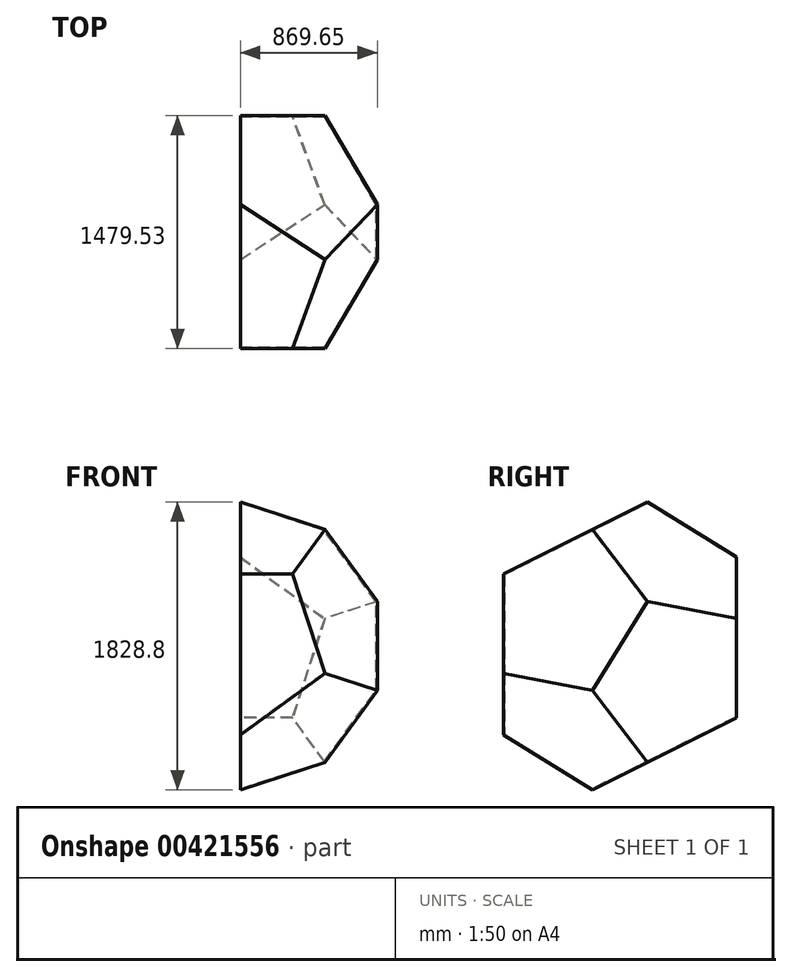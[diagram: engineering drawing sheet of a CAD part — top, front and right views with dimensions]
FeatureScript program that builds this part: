
annotation { "Feature Type Name" : "Feature", "Feature Type Description" : "" }
export const myFeature = defineFeature(function(context is Context, id is Id, definition is map)
    precondition{}
    {
        {
            var Q0;
            Q0=qCreatedBy(makeId("Front.planeOp"),FACE);
            var sketch = newSketch(context, id + "F0", { "sketchPlane" : qUnion([Q0])});
            skCircle(sketch, "E0.cCircle", {"center": v(0, 0) * mm, "radius": 1196.97 * mm, "construction": true});
            skLineSegment(sketch, "E0.0", {"start": v(1407.12, -457.2) * mm, "end": v(0, -1479.53) * mm});
            skLineSegment(sketch, "E0.1", {"start": v(0, -1479.53) * mm, "end": v(-1407.12, -457.2) * mm});
            skLineSegment(sketch, "E0.2", {"start": v(-1407.12, -457.2) * mm, "end": v(-869.65, 1196.97) * mm});
            skLineSegment(sketch, "E0.3", {"start": v(-869.65, 1196.97) * mm, "end": v(869.65, 1196.97) * mm});
            skLineSegment(sketch, "E0.4", {"start": v(869.65, 1196.97) * mm, "end": v(1407.12, -457.2) * mm});
            skLineSegment(sketch, "E1", {"start": v(-1407.12, -457.2) * mm, "end": v(1407.12, -457.2) * mm, "construction": true});
            skLineSegment(sketch, "E2", {"start": v(-1407.12, -457.2) * mm, "end": v(869.65, 1196.97) * mm, "construction": true});
            skLineSegment(sketch, "E3", {"start": v(-869.65, 1196.97) * mm, "end": v(0, -1479.53) * mm, "construction": true});
            skLineSegment(sketch, "E4", {"start": v(869.65, 1196.97) * mm, "end": v(0, -1479.53) * mm, "construction": true});
            skLineSegment(sketch, "E5", {"start": v(-869.65, 1196.97) * mm, "end": v(1407.12, -457.2) * mm, "construction": true});
            skCircle(sketch, "E6", {"center": v(0, 0) * mm, "radius": 457.2 * mm, "construction": true});
            skLineSegment(sketch, "E7", {"start": v(0, 0) * mm, "end": v(457.2, 0) * mm});
            skCircle(sketch, "E8", {"center": v(0, 0) * mm, "radius": 1479.53 * mm, "construction": true});
            skLineSegment(sketch, "E9", {"start": v(0, 0) * mm, "end": v(-1479.53, 0) * mm});
            skSolve(sketch);
        }
        {
            var Q0;
            Q0=qCreatedBy(makeId("Top.planeOp"),FACE);
            var sketch = newSketch(context, id + "F1", { "sketchPlane" : qUnion([Q0])});
            skLineSegment(sketch, "E10.0", {"start": v(0, 0) * mm, "end": v(-1479.53, 0) * mm});
            skLineSegment(sketch, "E11.0", {"start": v(0, 0) * mm, "end": v(457.2, 0) * mm});
            skLineSegment(sketch, "E12", {"start": v(-1479.53, 0) * mm, "end": v(0, -739.77) * mm});
            skLineSegment(sketch, "E13", {"start": v(-661.67, -408.93) * mm, "end": v(-457.2, 0) * mm});
            skLineSegment(sketch, "E14", {"start": v(0, 0) * mm, "end": v(0, -1479.53) * mm});
            skPoint(sketch, "E15", {"position": v(0, -739.77) * mm});
            skLineSegment(sketch, "E16", {"start": v(457.2, -1479.53) * mm, "end": v(-457.2, -1479.53) * mm});
            skLineSegment(sketch, "E17", {"start": v(-1196.97, 0) * mm, "end": v(0, -2393.93) * mm});
            skLineSegment(sketch, "E18", {"start": v(0, -739.77) * mm, "end": v(196.68, -739.77) * mm});
            skSolve(sketch);
        }
        {
            var Q0;
            Q0=makeQuery(id+"F0.imprint","IMPRINT",FACE,{"disambiguationData":[TD([[makeQuery(id+"F0.imprint","IMPRINT",EDGE,{"derivedFrom":sQuery(id+"F0.wireOp",EDGE,"E0.0")}),-1.0]])]});
            var Q1;
            Q1=sQuery(id+"F1.wireOp",VERTEX,"E17.end");
            loft(context, id + "F2", {"sheetProfilesArray" : [{ "sheetProfileEntities" : qUnion([Q0]) }, { "sheetProfileEntities" : qUnion([Q1]) }]});
        }
        {
            var Q0;
            Q0=makeQuery(id+"F2.opLoft","SWEPT_BODY",BODY,{"disambiguationData":[OSD([makeQuery(id+"F0.imprint","IMPRINT",FACE,{"disambiguationData":[TD([[makeQuery(id+"F0.imprint","IMPRINT",EDGE,{"derivedFrom":sQuery(id+"F0.wireOp",EDGE,"E0.0")}),-1.0]])]}),sQuery(id+"F1.wireOp",VERTEX,"Gg8BuWM7-8xwd-dMkX-fKB3-R5DVQcrtt8fb.end")])]});
            var Q1;
            Q1=sQuery(id+"F1.wireOp",EDGE,"E18");
            transform(context, id + "F3", {"entities" : qUnion([Q0]), "transformType" : TransformType.ROTATION, "transformAxis" : qUnion([Q1]), "angle" : 180 * degree, "makeCopy" : true});
        }
        {
            var Q0;
            Q0=makeQuery(id+"F2.opLoft","SWEPT_BODY",BODY,{"disambiguationData":[OSD([makeQuery(id+"F0.imprint","IMPRINT",FACE,{"disambiguationData":[TD([[makeQuery(id+"F0.imprint","IMPRINT",EDGE,{"derivedFrom":sQuery(id+"F0.wireOp",EDGE,"E0.0")}),-1.0]])]}),sQuery(id+"F1.wireOp",VERTEX,"Gg8BuWM7-8xwd-dMkX-fKB3-R5DVQcrtt8fb.end")])]});
            var Q1;
            Q1=makeQuery(id+"F3.opPattern","COPY",BODY,{"derivedFrom":makeQuery(id+"F2.opLoft","SWEPT_BODY",BODY,{"disambiguationData":[OSD([makeQuery(id+"F0.imprint","IMPRINT",FACE,{"disambiguationData":[TD([[makeQuery(id+"F0.imprint","IMPRINT",EDGE,{"derivedFrom":sQuery(id+"F0.wireOp",EDGE,"E0.0")}),-1.0]])]}),sQuery(id+"F1.wireOp",VERTEX,"Gg8BuWM7-8xwd-dMkX-fKB3-R5DVQcrtt8fb.end")])]}),"instanceName":"1"});
            booleanBodies(context, id + "F4", {"operationType" : BooleanOperationType.INTERSECTION, "tools" : qUnion([Q0, Q1])});
        }
        {
            var Q0;
            Q0=makeQuery(id+"F2.opLoft","CAP_FACE",FACE,{"disambiguationData":[OSD([makeQuery(id+"F0.imprint","IMPRINT",FACE,{"disambiguationData":[TD([[makeQuery(id+"F0.imprint","IMPRINT",EDGE,{"derivedFrom":sQuery(id+"F0.wireOp",EDGE,"E0.0")}),-1.0]])]})])],"isStart":true});
            var sketch = newSketch(context, id + "F5", { "sketchPlane" : qUnion([Q0])});
            skLineSegment(sketch, "E19", {"start": v(0, 565.13) * mm, "end": v(0, -387.37) * mm});
            skLineSegment(sketch, "E20", {"start": v(0, 565.13) * mm, "end": v(0, -281.45) * mm});
            skSolve(sketch);
        }
        {
            var Q0;
            Q0=sQuery(id+"F5.wireOp",VERTEX,"E19.start");
            var Q1;
            {var subQ0=sQuery(id+"F0.wireOp",EDGE,"E0.2");var subQ1=sQuery(id+"F0.wireOp",EDGE,"E0.1");var subQ2=sQuery(id+"F0.wireOp",EDGE,"E0.0");var subQ3=sQuery(id+"F0.wireOp",EDGE,"E0.4");Q1=makeQuery(id+"F4.opBoolean","INTERSECT",VERTEX,{"derivedFrom":[makeQuery(id+"F2.opLoft","SWEPT_FACE",FACE,{"disambiguationData":[OSD([subQ0,sQuery(id+"F0.wireOp",EDGE,"E0.3"),subQ3])]}),makeQuery(id+"F3.opPattern","COPY",FACE,{"derivedFrom":makeQuery(id+"F2.opLoft","SWEPT_FACE",FACE,{"disambiguationData":[OSD([subQ2,subQ1,subQ3])]}),"instanceName":"1"}),makeQuery(id+"F3.opPattern","COPY",FACE,{"derivedFrom":makeQuery(id+"F2.opLoft","SWEPT_FACE",FACE,{"disambiguationData":[OSD([subQ2,subQ1,subQ0])]}),"instanceName":"1"})]});}
            var Q2;
            {var subQ1=sQuery(id+"F0.wireOp",EDGE,"E0.2");var subQ2=sQuery(id+"F0.wireOp",EDGE,"E0.1");var subQ3=sQuery(id+"F0.wireOp",EDGE,"E0.0");var subQ4=sQuery(id+"F0.wireOp",EDGE,"E0.4");Q2=makeQuery(id+"F4.opBoolean","INTERSECT",VERTEX,{"derivedFrom":[makeQuery(id+"F2.opLoft","SWEPT_FACE",FACE,{"disambiguationData":[OSD([subQ3,subQ2,subQ4])]}),makeQuery(id+"F2.opLoft","SWEPT_FACE",FACE,{"disambiguationData":[OSD([subQ3,subQ2,subQ1])]}),makeQuery(id+"F3.opPattern","COPY",FACE,{"derivedFrom":makeQuery(id+"F2.opLoft","CAP_FACE",FACE,{"disambiguationData":[OSD([makeQuery(id+"F0.imprint","IMPRINT",FACE,{"disambiguationData":[TD([[makeQuery(id+"F0.imprint","IMPRINT",EDGE,{"derivedFrom":subQ3}),-1.0]])]})])],"isStart":true}),"instanceName":"1"})]});}
            cPlane(context, id + "F6", {"entities" : qUnion([Q0, Q1, Q2]), "cplaneType" : CPlaneType.THREE_POINT, "offset" : 25.4 * mm, "width" : 152.4 * mm, "height" : 152.4 * mm});
        }
        {
            var Q0;
            Q0=qCreatedBy(id+"F6.planeOp",FACE);
            var sketch = newSketch(context, id + "F7", { "sketchPlane" : qUnion([Q0])});
            skLineSegment(sketch, "E21.0", {"start": v(565.13, 914.4) * mm, "end": v(0, 565.13) * mm});
            skLineSegment(sketch, "E22.0", {"start": v(914.4, -914.4) * mm, "end": v(1479.53, -565.13) * mm});
            skLineSegment(sketch, "E23.0", {"start": v(0, 565.13) * mm, "end": v(0, -281.45) * mm});
            skLineSegment(sketch, "E24", {"start": v(565.13, 914.4) * mm, "end": v(1479.53, 457.2) * mm});
            skLineSegment(sketch, "E25", {"start": v(1479.53, 457.2) * mm, "end": v(1479.53, -565.13) * mm});
            skLineSegment(sketch, "E26", {"start": v(0, -281.45) * mm, "end": v(914.4, -914.4) * mm});
            skLineSegment(sketch, "E27.0", {"start": v(549.44, 1263.02) * mm, "end": v(-304.8, 735.07) * mm});
            skLineSegment(sketch, "E27.1", {"start": v(1784.33, 645.58) * mm, "end": v(1784.33, -735.07) * mm});
            skLineSegment(sketch, "E27.2", {"start": v(904.95, -1278.56) * mm, "end": v(1784.33, -735.07) * mm});
            skLineSegment(sketch, "E27.3", {"start": v(549.44, 1263.02) * mm, "end": v(1784.33, 645.58) * mm});
            skLineSegment(sketch, "E27.4", {"start": v(-304.8, -441.17) * mm, "end": v(904.95, -1278.56) * mm});
            skLineSegment(sketch, "E27.5", {"start": v(-304.8, 735.07) * mm, "end": v(-304.8, -441.17) * mm});
            skSolve(sketch);
        }
        {
            var Q0;
            Q0=makeQuery(id+"F7.imprint","IMPRINT",FACE,{"disambiguationData":[TD([[makeQuery(id+"F7.imprint","IMPRINT",EDGE,{"derivedFrom":sQuery(id+"F7.wireOp",EDGE,"E21.0")}),1.0]])]});
            var Q1;
            Q1=makeQuery(id+"F7.imprint","IMPRINT",FACE,{"disambiguationData":[TD([[makeQuery(id+"F7.imprint","IMPRINT",EDGE,{"derivedFrom":sQuery(id+"F7.wireOp",EDGE,"E21.0")}),-1.0]])]});
            extrude(context, id + "F8", {"entities" : qUnion([Q0, Q1]), "operationType" : NewBodyOperationType.REMOVE, "endBound" : BoundingType.THROUGH_ALL, "depth" : 25.4 * mm, "offsetDistance" : 25.4 * mm});
        }
        {
            var Q0;
            Q0=makeQuery(id+"F8.boolean.opBoolean","COPY",FACE,{"derivedFrom":makeQuery(id+"F8.opExtrude","CAP_FACE",FACE,{"disambiguationData":[OSD([sQuery(id+"F7.wireOp",EDGE,"E27.0"),sQuery(id+"F7.wireOp",EDGE,"E27.1"),sQuery(id+"F7.wireOp",EDGE,"E27.2"),sQuery(id+"F7.wireOp",EDGE,"E27.3"),sQuery(id+"F7.wireOp",EDGE,"E27.4"),sQuery(id+"F7.wireOp",EDGE,"E27.5")])],"isStart":true})});
            shell(context, id + "F9", {"entities" : qUnion([Q0]), "thickness" : 6.35 * mm});
        }
    });
